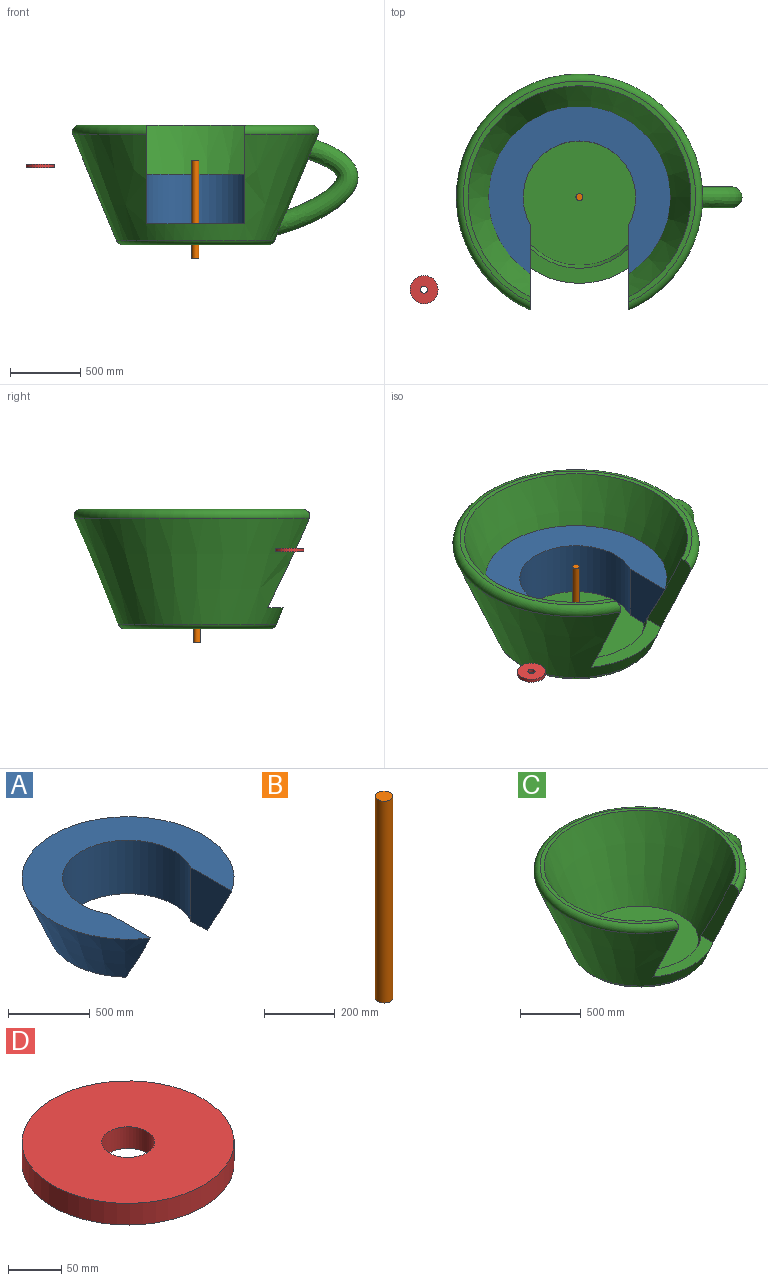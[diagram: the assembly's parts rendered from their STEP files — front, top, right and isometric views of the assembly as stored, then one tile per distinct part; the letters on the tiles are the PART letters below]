
ASSEMBLY  parts=4 mates=2
PART A: 6 faces, bbox 1295.5x1192.8x400 mm
  f0: plane 966.06x815.93mm, normal (0,0,-1), area 162980.2mm2, adj f2,f3,f4,f5
  f1: plane 1295.47x1192.77mm, normal (0,0,1), area 623420mm2, adj f2,f3,f4,f5
  f2: plane 400.01x351.39mm, normal (1,0,0), area 99493.2mm2, adj f0,f1,f4,f5
  f3: plane 400.01x351.39mm, normal (-1,0,0), area 99493.2mm2, adj f0,f1,f4,f5
  f4: cylinder r=400mm len=800mm, axis (0,0,1), area 664370.2mm2, adj f0,f1,f2,f3
  f5: cone r=807.53mm half-angle=22.4deg, axis (0,0,1), area 1209297.4mm2, adj f0,f1,f2,f3
PART B: 3 faces, bbox 50x50x700 mm
  f0: cylinder r=25mm len=700mm, axis (0,0,-1), area 109955.7mm2, adj f1,f2
  f1: plane 50x50mm, normal (0,0,1), area 1963.5mm2, adj f0
  f2: plane 50x50mm, normal (0,0,-1), area 1963.5mm2, adj f0
PART C: 12 faces, bbox 2103.1x1819x850 mm
  f0: plane 1650.68x1572.79mm, normal (0,0,1), area 145879.6mm2, adj f2,f3,f9,f10
  f1: cone r=900mm half-angle=22.4deg, axis (0,0,1), area 3116241.3mm2, adj f3,f5,f7,f8,f9,f10
  f2: cone r=807.53mm half-angle=22.4deg, axis (0,0,1), area 2686379.6mm2, adj f0,f6,f8,f9,f10
  f3: torus R=825.34mm, axis (0,0,1), area 459555.1mm2, adj f0,f1,f9,f10
  f4: plane 1033.03x1033.03mm, normal (0,0,-1), area 836176.1mm2, adj f7,f11
  f5: bspline ~750.61x682.88mm, area 438367.2mm2, adj f1
  f6: plane 966.06x966.06mm, normal (0,0,1), area 731028.8mm2, adj f2,f11
  f7: torus R=516.52mm, axis (0,0,1), area 201234.2mm2, adj f1,f4
  f8: plane 700x249.64mm, normal (0,0,1), area 81938.6mm2, adj f1,f2,f9,f10
  f9: plane 700.02x440.22mm, normal (1,0,0), area 86992.6mm2, adj f0,f1,f2,f3,f8
  f10: plane 700.02x440.22mm, normal (-1,0,0), area 86992.6mm2, adj f0,f1,f2,f3,f8
  f11: cylinder r=25mm len=100mm, axis (0,0,-1), area 15708mm2, adj f4,f6
PART D: 4 faces, bbox 200x200x25 mm
  f0: cylinder r=25mm len=50mm, axis (0,0,1), area 3927mm2, adj f2,f3
  f1: cylinder r=100mm len=200mm, axis (0,0,1), area 15708mm2, adj f2,f3
  f2: plane 200x200mm, normal (0,0,-1), area 29452.4mm2, adj f0,f1
  f3: plane 200x200mm, normal (0,0,1), area 29452.4mm2, adj f0,f1
PLACE A at identity
PLACE B t=(0,0,-50)mm
PLACE C at identity fixed
PLACE D t=(-1105.01,-657.51,-79.3)mm
MATE fastened C.f1 <-> A.f4  axis (0,0,1) through (0,0,100)mm
MATE fastened B.f0 <-> C.f1  axis (0,0,-1) through (0,0,-100)mm
